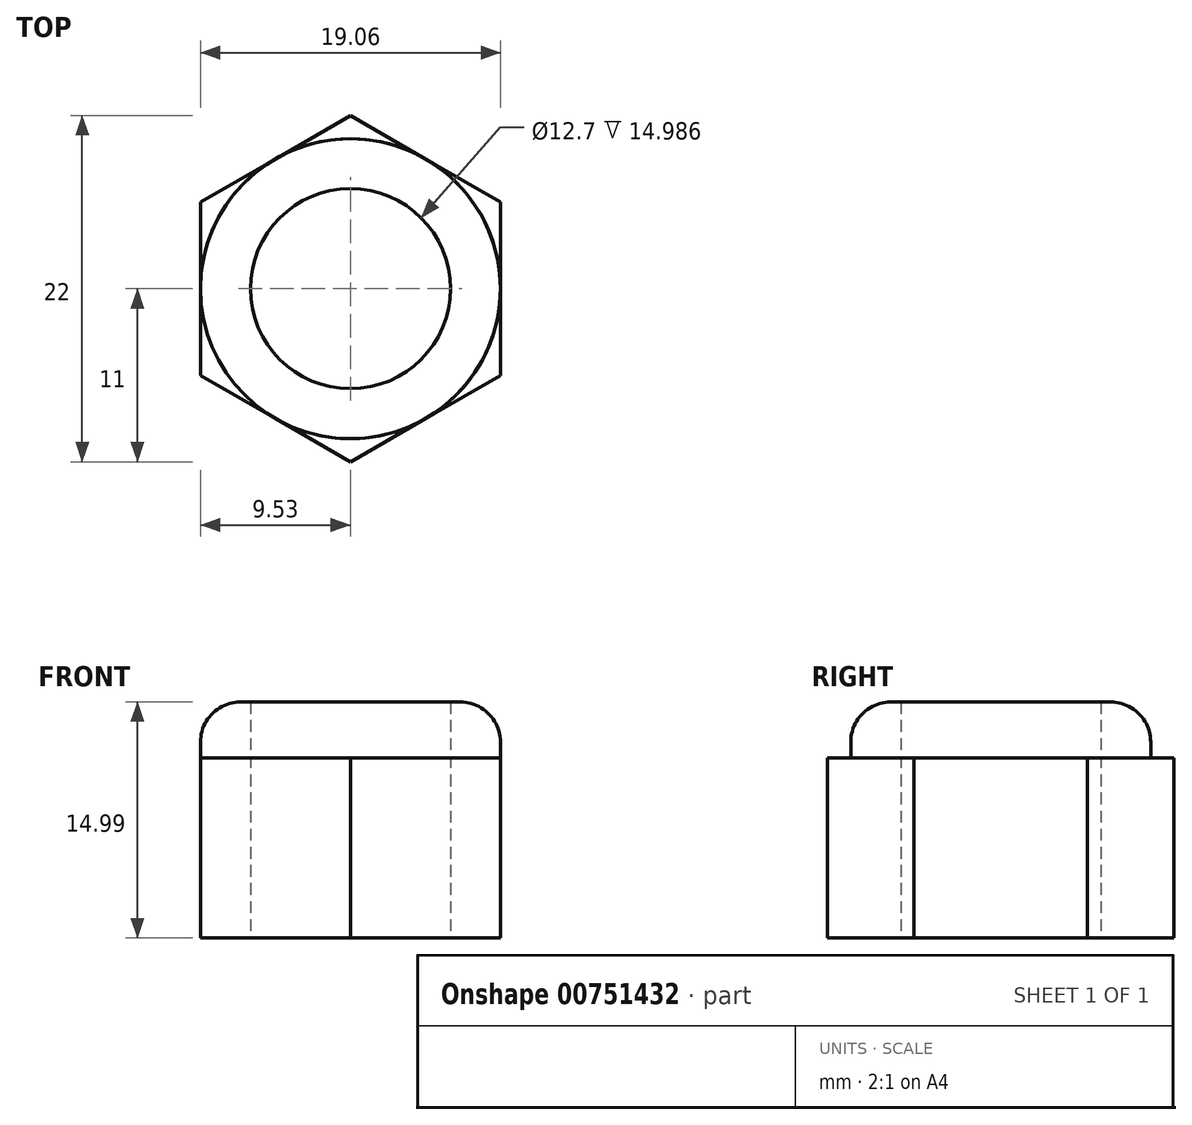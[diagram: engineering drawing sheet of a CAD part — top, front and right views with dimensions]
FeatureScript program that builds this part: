
annotation { "Feature Type Name" : "Feature", "Feature Type Description" : "" }
export const myFeature = defineFeature(function(context is Context, id is Id, definition is map)
    precondition{}
    {
        {
            var Q0;
            Q0=qCreatedBy(makeId("Top.planeOp"),FACE);
            var sketch = newSketch(context, id + "F0", { "sketchPlane" : qUnion([Q0])});
            skCircle(sketch, "E0.cCircle", {"center": v(0, 0) * mm, "radius": 9.53 * mm});
            skLineSegment(sketch, "E0.0", {"start": v(9.53, 5.5) * mm, "end": v(9.53, -5.5) * mm});
            skLineSegment(sketch, "E0.1", {"start": v(9.53, -5.5) * mm, "end": v(0, -11) * mm});
            skLineSegment(sketch, "E0.2", {"start": v(0, -11) * mm, "end": v(-9.52, -5.5) * mm});
            skLineSegment(sketch, "E0.3", {"start": v(-9.52, -5.5) * mm, "end": v(-9.53, 5.5) * mm});
            skLineSegment(sketch, "E0.4", {"start": v(-9.53, 5.5) * mm, "end": v(0, 11) * mm});
            skLineSegment(sketch, "E0.5", {"start": v(0, 11) * mm, "end": v(9.52, 5.5) * mm});
            skPoint(sketch, "E0.0.midPoint", {"position": v(9.53, 0) * mm});
            skCircle(sketch, "E1", {"center": v(0, 0) * mm, "radius": 6.35 * mm});
            skSolve(sketch);
        }
        {
            var Q0;
            Q0=makeQuery(id+"F0.imprint","IMPRINT",FACE,{"disambiguationData":[TD([[makeQuery(id+"F0.imprint","IMPRINT",EDGE,{"derivedFrom":sQuery(id+"F0.wireOp",EDGE,"E1")}),-1.0]])]});
            var Q1;
            {var subQ0=sQuery(id+"F0.wireOp",EDGE,"E0.4");var subQ1=sQuery(id+"F0.wireOp",EDGE,"E0.cCircle");var subQ2=makeQuery(id+"F0.imprint","INTERSECT",VERTEX,{"derivedFrom":[subQ1,subQ0]});Q1=makeQuery(id+"F0.imprint","IMPRINT",FACE,{"disambiguationData":[TD([[makeQuery(id+"F0.imprint","IMPRINT",EDGE,{"disambiguationData":[TD([[subQ2,-1.0]])],"derivedFrom":subQ1}),-1.0]])]});}
            var Q2;
            {var subQ0=sQuery(id+"F0.wireOp",EDGE,"E0.5");var subQ1=sQuery(id+"F0.wireOp",EDGE,"E0.cCircle");var subQ2=makeQuery(id+"F0.imprint","INTERSECT",VERTEX,{"derivedFrom":[subQ1,subQ0]});Q2=makeQuery(id+"F0.imprint","IMPRINT",FACE,{"disambiguationData":[TD([[makeQuery(id+"F0.imprint","IMPRINT",EDGE,{"disambiguationData":[TD([[subQ2,-1.0]])],"derivedFrom":subQ1}),-1.0]])]});}
            var Q3;
            {var subQ0=sQuery(id+"F0.wireOp",EDGE,"E0.5");var subQ1=sQuery(id+"F0.wireOp",EDGE,"E0.cCircle");var subQ2=makeQuery(id+"F0.imprint","INTERSECT",VERTEX,{"derivedFrom":[subQ1,subQ0]});Q3=makeQuery(id+"F0.imprint","IMPRINT",FACE,{"disambiguationData":[TD([[makeQuery(id+"F0.imprint","IMPRINT",EDGE,{"disambiguationData":[TD([[subQ2,1.0]])],"derivedFrom":subQ1}),-1.0]])]});}
            var Q4;
            {var subQ0=sQuery(id+"F0.wireOp",EDGE,"E0.0");var subQ1=sQuery(id+"F0.wireOp",EDGE,"E0.cCircle");var subQ2=makeQuery(id+"F0.imprint","INTERSECT",VERTEX,{"derivedFrom":[subQ1,subQ0]});Q4=makeQuery(id+"F0.imprint","IMPRINT",FACE,{"disambiguationData":[TD([[makeQuery(id+"F0.imprint","IMPRINT",EDGE,{"disambiguationData":[TD([[subQ2,1.0]])],"derivedFrom":subQ1}),-1.0]])]});}
            var Q5;
            {var subQ0=sQuery(id+"F0.wireOp",EDGE,"E0.2");var subQ1=sQuery(id+"F0.wireOp",EDGE,"E0.cCircle");var subQ2=makeQuery(id+"F0.imprint","INTERSECT",VERTEX,{"derivedFrom":[subQ1,subQ0]});Q5=makeQuery(id+"F0.imprint","IMPRINT",FACE,{"disambiguationData":[TD([[makeQuery(id+"F0.imprint","IMPRINT",EDGE,{"disambiguationData":[TD([[subQ2,-1.0]])],"derivedFrom":subQ1}),-1.0]])]});}
            var Q6;
            {var subQ0=sQuery(id+"F0.wireOp",EDGE,"E0.3");var subQ1=sQuery(id+"F0.wireOp",EDGE,"E0.cCircle");var subQ2=makeQuery(id+"F0.imprint","INTERSECT",VERTEX,{"derivedFrom":[subQ1,subQ0]});Q6=makeQuery(id+"F0.imprint","IMPRINT",FACE,{"disambiguationData":[TD([[makeQuery(id+"F0.imprint","IMPRINT",EDGE,{"disambiguationData":[TD([[subQ2,-1.0]])],"derivedFrom":subQ1}),-1.0]])]});}
            extrude(context, id + "F1", {"entities" : qUnion([Q0, Q1, Q2, Q3, Q4, Q5, Q6]), "depth" : 11.43 * mm, "offsetDistance" : 25.4 * mm});
        }
        {
            var Q0;
            Q0=makeQuery(id+"F0.imprint","IMPRINT",FACE,{"disambiguationData":[TD([[makeQuery(id+"F0.imprint","IMPRINT",EDGE,{"derivedFrom":sQuery(id+"F0.wireOp",EDGE,"E1")}),-1.0]])]});
            extrude(context, id + "F2", {"entities" : qUnion([Q0]), "operationType" : NewBodyOperationType.ADD, "depth" : 15 * mm, "offsetDistance" : 25.4 * mm});
        }
        {
            var Q0;
            Q0=makeQuery(id+"F2.opExtrude","CAP_EDGE",EDGE,{"disambiguationData":[OSD([sQuery(id+"F0.wireOp",EDGE,"E0.cCircle")])],"isStart":false});
            fillet(context, id + "F3", {"entities" : qUnion([Q0]), "radius" : 2.54 * mm, "tangentPropagation" : true, "allowEdgeOverflow" : false});
        }
    });
